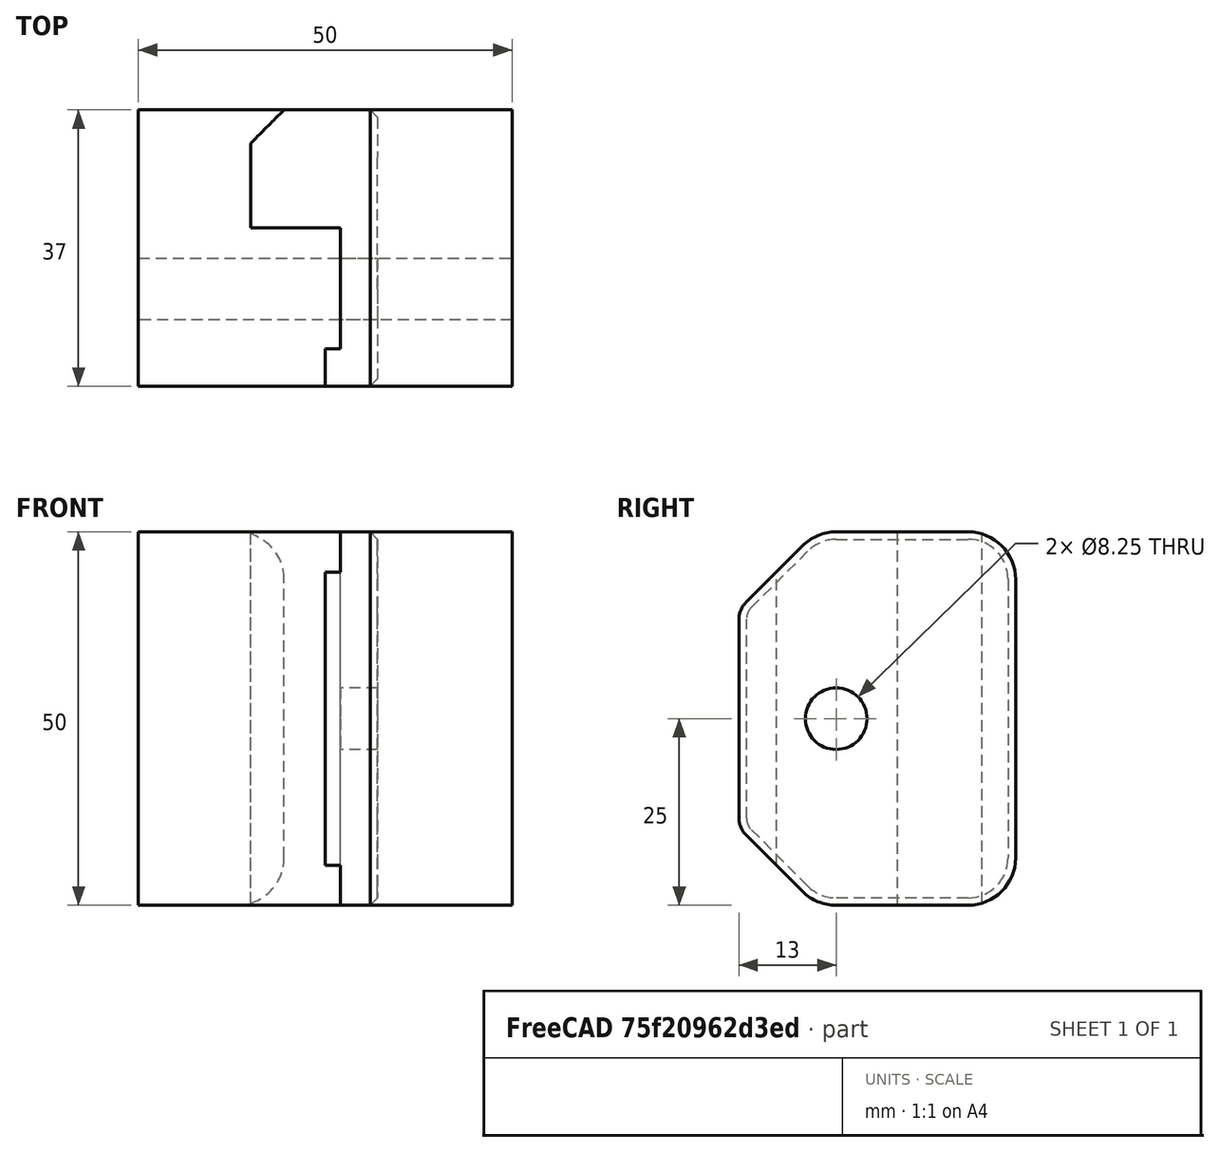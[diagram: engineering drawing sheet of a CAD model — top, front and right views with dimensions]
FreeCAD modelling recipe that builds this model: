
FCSTD DOCUMENT  (FreeCAD 0.19R23578 (Git))
Label: z_rail_clamp
License: All rights reserved
LicenseURL: http://en.wikipedia.org/wiki/All_rights_reserved
objects: TechDraw::DrawViewDimension×14, TechDraw::DrawProjGroupItem×3, Sketcher::SketchObject×2, PartDesign::Pad×2, PartDesign::Body×2, PartDesign::Boolean×1, PartDesign::Chamfer×1, App::Part×1, TechDraw::DrawSVGTemplate×1, TechDraw::DrawViewPart×1, TechDraw::DrawProjGroup×1, TechDraw::DrawPage×1
note: 11 computed .brp shape members not serialized (recipe doc carries the construction recipe); baked Part::Feature solids carry a one-line shape summary decoded from their .brp

FEATURE [Sketcher::SketchObject] Sketch073
  MapMode = 5
  Support = -> [XY_Plane086]
  sketch-geometry (14):
    g0: LineSegment StartX=0 StartY=0 StartZ=0 EndX=0 EndY=-9.5892e-11 EndZ=0
    g1: LineSegment StartX=0 StartY=0 StartZ=0 EndX=-18 EndY=0 EndZ=0
    g2: LineSegment StartX=-18 StartY=0 StartZ=0 EndX=-18 EndY=20 EndZ=0
    g3: LineSegment StartX=-18 StartY=20 StartZ=0 EndX=0 EndY=20 EndZ=0
    g4: Circle CenterX=-12 CenterY=14 CenterZ=0 NormalX=0 NormalY=0 NormalZ=1 AngleXU=0 Radius=6
    g5: LineSegment StartX=7 StartY=12 StartZ=0 EndX=-5.51472 EndY=12 EndZ=0
    g6: LineSegment StartX=-5.51472 StartY=12 StartZ=0 EndX=-10 EndY=7.51472 EndZ=0
    g7: LineSegment StartX=-10 StartY=7.51472 StartZ=0 EndX=-10 EndY=-3.8 EndZ=0
    g8: LineSegment StartX=-10 StartY=-3.8 StartZ=0 EndX=2 EndY=-3.8 EndZ=0
    g9: LineSegment StartX=2 StartY=-3.8 StartZ=0 EndX=2 EndY=-20 EndZ=0
    g10: LineSegment StartX=2 StartY=-20 StartZ=0 EndX=0 EndY=-20 EndZ=0
    g11: LineSegment StartX=0 StartY=-20 StartZ=0 EndX=0 EndY=-40 EndZ=0
    g12: LineSegment StartX=0 StartY=-40 StartZ=0 EndX=7 EndY=-40 EndZ=0
    g13: LineSegment StartX=7 StartY=-40 StartZ=0 EndX=7 EndY=12 EndZ=0
  constraints (41):
    c: Coincident(g0,g-1)
    c: Coincident(g1,g-1)
    c: PointOnObject(g1,g-1)
    c: Coincident(g2,g1)
    c: Vertical(g2)
    c: Coincident(g3,g2)
    c: PointOnObject(g3,g-2)
    c: Horizontal(g3)
    c: Tangent(g4,g3)
    c: Tangent(g4,g2)
    c: Diameter(g4) = 12
    c: DistanceX(g3,g3) = 18
    c: DistanceY(g2,g2) = 20
    c: Horizontal(g5)
    c: Coincident(g5,g6)
    c: Tangent(g6,g4)
    c: Coincident(g6,g7)
    c: Vertical(g7)
    c: Coincident(g7,g8)
    c: Horizontal(g8)
    c: Coincident(g8,g9)
    c: Vertical(g9)
    c: Coincident(g9,g10)
    c: Horizontal(g10)
    c: Coincident(g10,g11)
    c: Coincident(g11,g12)
    c: Horizontal(g12)
    c: Coincident(g12,g13)
    c: Coincident(g13,g5)
    c: Vertical(g13)
    c: Angle(g8,g6) = 0.785398
    c: DistanceY(g-1,g5) = 12
    c: DistanceX(g10,g10) = 2
    c: DistanceX(g12,g12) = 7
    c: DistanceY(g9,g9) = 16.2
    c: DistanceY(g11,g11) = 20
    c: Coincident(g0,g-1)
    c: Vertical(g11)
    c: PointOnObject(g10,g-2)
    c: DistanceX(g7,g-1) = 10
    c: DistanceY(g7,g2) = 23.8
FEATURE [PartDesign::Pad] Pad027  label="Pad028"
  Direction = (1,1,1)
  Length = 100
  Length2 = 100
  Midplane = true
  Profile = -> Sketch073
  Type = 0
FEATURE [Sketcher::SketchObject] Sketch074
  MapMode = 5
  Placement = pos=(0,0,0) rot=(0.57735,0.57735,0.57735;2.0944rad)
  Support = -> [YZ_Plane085]
  sketch-geometry (13):
    g0: LineSegment StartX=12 StartY=18.65 StartZ=0 EndX=12 EndY=-18.65 EndZ=0
    g1: LineSegment StartX=5.65 StartY=-25 StartZ=0 EndX=-12 EndY=-25 EndZ=0
    g2: LineSegment StartX=-16.4901 StartY=-23.1401 StartZ=0 EndX=-24.092 EndY=-15.5382 EndZ=0
    g3: LineSegment StartX=-24.092 StartY=15.5382 StartZ=0 EndX=-16.4901 EndY=23.1401 EndZ=0
    g4: LineSegment StartX=-12 StartY=25 StartZ=0 EndX=5.65 EndY=25 EndZ=0
    g5: ArcOfCircle CenterX=5.65 CenterY=18.65 CenterZ=0 NormalX=0 NormalY=0 NormalZ=1 AngleXU=0 Radius=6.35 StartAngle=0 EndAngle=1.5708
    g6: ArcOfCircle CenterX=-12 CenterY=18.65 CenterZ=0 NormalX=0 NormalY=0 NormalZ=1 AngleXU=0 Radius=6.35 StartAngle=1.5708 EndAngle=2.35619
    g7: ArcOfCircle CenterX=-12 CenterY=-18.65 CenterZ=0 NormalX=0 NormalY=0 NormalZ=1 AngleXU=0 Radius=6.35 StartAngle=3.92699 EndAngle=4.71239
    g8: ArcOfCircle CenterX=5.65 CenterY=-18.65 CenterZ=0 NormalX=0 NormalY=0 NormalZ=1 AngleXU=0 Radius=6.35 StartAngle=4.71239 EndAngle=6.28319
    g9: Circle CenterX=-12 CenterY=0 CenterZ=0 NormalX=0 NormalY=0 NormalZ=1 AngleXU=0 Radius=4.125
    g10: LineSegment StartX=-25 StartY=13.3462 StartZ=0 EndX=-25 EndY=-13.3462 EndZ=0
    g11: ArcOfCircle CenterX=-21.9 CenterY=13.3462 CenterZ=0 NormalX=0 NormalY=0 NormalZ=1 AngleXU=0 Radius=3.1 StartAngle=2.35619 EndAngle=3.14159
    g12: ArcOfCircle CenterX=-21.9 CenterY=-13.3462 CenterZ=0 NormalX=0 NormalY=0 NormalZ=1 AngleXU=0 Radius=3.1 StartAngle=3.14159 EndAngle=3.92699
  constraints (30):
    c: Vertical(g0)
    c: Horizontal(g1)
    c: Tangent(g4,g5) = 1.5708
    c: Tangent(g0,g5) = 1.5708
    c: Tangent(g4,g6) = 1.5708
    c: Tangent(g3,g6) = 1.5708
    c: Tangent(g2,g7) = 1.5708
    c: Tangent(g1,g7) = 1.5708
    c: Tangent(g0,g8) = 1.5708
    c: Tangent(g1,g8) = 1.5708
    c: Horizontal(g4)
    c: Equal(g7,g8)
    c: Symmetric(g4,g1,g-1)
    c: Symmetric(g6,g7,g-1)
    c: PointOnObject(g9,g-1)
    c: DistanceY(g1,g4) = 50
    c: Radius(g5) = 6.35
    c: Diameter(g9) = 8.25
    c: DistanceX(g-1,g0) = 12
    c: Angle(g2,g3) = 1.5708
    c: Vertical(g10)
    c: Tangent(g3,g11) = 1.5708
    c: Tangent(g10,g11) = -1.5708
    c: Tangent(g10,g12) = -1.5708
    c: Tangent(g2,g12) = 1.5708
    c: Radius(g11) = 3.1
    c: Symmetric(g11,g12,g-1)
    c: DistanceX(g10,g-1) = 25
    c: Vertical(g7,g9)
    c: DistanceX(g9,g-1) = 12
FEATURE [PartDesign::Pad] Pad028  label="Pad029"
  Direction = (1,1,1)
  Length = 50
  Length2 = 100
  Midplane = true
  Placement = pos=(0,0,0) rot=(0.57735,0.57735,0.57735;2.0944rad)
  Profile = -> Sketch074
  Type = 0
FEATURE [PartDesign::Body] Body028
  Group = -> [Sketch074,Pad028]
  Origin = -> Origin085
  Tip = -> Pad028
FEATURE [PartDesign::Boolean] Boolean002
  BaseFeature = -> Pad027
  Group = -> [Body028]
  Type = 2
FEATURE [PartDesign::Chamfer] Chamfer002
  Angle = 45
  Base = -> Boolean002 [Edge14]
  BaseFeature = -> Boolean002
  ChamferType = 0
  FlipDirection = false
  Size = 1
  Size2 = 1
  SupportTransform = true
FEATURE [PartDesign::Body] Body029  label="Body"
  Group = -> [Sketch073,Pad027,Boolean002,Chamfer002]
  Origin = -> Origin086
  Tip = -> Chamfer002
FEATURE [App::Part] Part044  label="z_rail_clamp"
  Group = -> [Body029]
  Origin = -> Origin082
FEATURE [TechDraw::DrawSVGTemplate] Template003
  EditableTexts = Author=Alex Neufeld; DWG_num=2020-102; Date=15/05/2020; Revision=2; Scale=NTS; Subtitle=4 Req.; Title=12mm Shaft Clamp
  Height = 215.9
  Orientation = 1
  Width = 279.4
FEATURE [TechDraw::DrawViewPart] View003
  CoarseView = false
  Direction = (0.577,-0.577,0.577)
  Focus = 100
  HardHidden = false
  IsoCount = 0
  IsoHidden = false
  IsoVisible = false
  LockPosition = false
  Perspective = false
  Rotation = 0
  Scale = 0.5
  ScaleType = 0
  SeamHidden = false
  SeamVisible = true
  SmoothHidden = false
  SmoothVisible = true
  Source = -> [Body029]
  X = 33.5005
  XDirection = (0.707,0.707,0)
  Y = 183.223
FEATURE [TechDraw::DrawProjGroupItem] ProjItem014  label="Front003"
  CoarseView = false
  Direction = (1,0,0)
  Focus = 100
  HardHidden = false
  IsoCount = 0
  IsoHidden = false
  IsoVisible = false
  LockPosition = true
  Perspective = false
  Rotation = 0
  RotationVector = (0,1,0)
  ScaleType = 2
  SeamHidden = false
  SeamVisible = true
  SmoothHidden = false
  SmoothVisible = true
  Source = -> [Body029]
  Type = 0
  X = 0
  XDirection = (0,1,0)
  Y = 0
FEATURE [TechDraw::DrawProjGroupItem] ProjItem015  label="Bottom003"
  CoarseView = false
  Direction = (0,0,-1)
  Focus = 100
  HardHidden = false
  IsoCount = 0
  IsoHidden = false
  IsoVisible = false
  LockPosition = false
  Perspective = false
  Rotation = 0
  RotationVector = (1,0,0)
  ScaleType = 2
  SeamHidden = false
  SeamVisible = true
  SmoothHidden = false
  SmoothVisible = true
  Source = -> [Body029]
  Type = 5
  X = 0
  XDirection = (0,1,0)
  Y = 48.5
FEATURE [TechDraw::DrawProjGroupItem] ProjItem016  label="Left002"
  CoarseView = false
  Direction = (1e-16,-1,0)
  Focus = 100
  HardHidden = false
  IsoCount = 0
  IsoHidden = false
  IsoVisible = false
  LockPosition = false
  Perspective = false
  Rotation = 0
  RotationVector = (1,0,0)
  ScaleType = 2
  SeamHidden = false
  SeamVisible = true
  SmoothHidden = false
  SmoothVisible = true
  Source = -> [Body029]
  Type = 1
  X = 42
  XDirection = (1,1e-16,0)
  Y = 0
FEATURE [TechDraw::DrawProjGroup] ProjGroup003
  Anchor = -> ProjItem014
  AutoDistribute = true
  LockPosition = false
  ProjectionType = 0
  Rotation = 0
  ScaleType = 0
  Source = -> [Body029]
  Views = -> [ProjItem014,ProjItem015,ProjItem016]
  X = 116.598
  Y = 88.1517
  spacingX = 15
  spacingY = 15
FEATURE [TechDraw::DrawViewDimension] Dimension065
  Arbitrary = false
  ArbitraryTolerances = false
  FormatSpec = %.2f
  FormatSpecOverTolerance = %+.2f
  FormatSpecUnderTolerance = %+.2f
  Inverted = false
  LockPosition = false
  MeasureType = 1
  OverTolerance = 0
  References2D = -> [ProjItem014]
  Rotation = 0
  ScaleType = 0
  TheoreticalExact = false
  Type = 2
  UnderTolerance = 0
  X = -37.8717
  Y = 1.13496
FEATURE [TechDraw::DrawViewDimension] Dimension066
  Arbitrary = false
  ArbitraryTolerances = false
  FormatSpec = %.2f
  FormatSpecOverTolerance = %+.2f
  FormatSpecUnderTolerance = %+.2f
  Inverted = false
  LockPosition = false
  MeasureType = 1
  OverTolerance = 0
  References2D = -> [ProjItem014]
  Rotation = 0
  ScaleType = 0
  TheoreticalExact = false
  Type = 1
  UnderTolerance = 0
  X = 0.243131
  Y = 37.6367
FEATURE [TechDraw::DrawViewDimension] Dimension067
  Arbitrary = false
  ArbitraryTolerances = false
  FormatSpec = %.2f
  FormatSpecOverTolerance = %+.2f
  FormatSpecUnderTolerance = %+.2f
  Inverted = false
  LockPosition = false
  MeasureType = 1
  OverTolerance = 0
  References2D = -> [ProjItem016]
  Rotation = 0
  ScaleType = 0
  TheoreticalExact = false
  Type = 1
  UnderTolerance = 0
  X = 0
  Y = 39.0878
FEATURE [TechDraw::DrawViewDimension] Dimension071
  Arbitrary = false
  ArbitraryTolerances = false
  FormatSpec = R%.2f
  FormatSpecOverTolerance = %+.2f
  FormatSpecUnderTolerance = %+.2f
  Inverted = false
  LockPosition = false
  MeasureType = 1
  OverTolerance = 0
  References2D = -> [ProjItem014]
  Rotation = 0
  ScaleType = 0
  TheoreticalExact = false
  Type = 4
  UnderTolerance = 0
  X = 26.3188
  Y = -26.8506
FEATURE [TechDraw::DrawViewDimension] Dimension072
  Arbitrary = false
  ArbitraryTolerances = false
  FormatSpec = %.2f
  FormatSpecOverTolerance = %+.2f
  FormatSpecUnderTolerance = %+.2f
  Inverted = false
  LockPosition = false
  MeasureType = 1
  OverTolerance = 0
  References2D = -> [ProjItem014]
  Rotation = 0
  ScaleType = 0
  TheoreticalExact = false
  Type = 2
  UnderTolerance = 0
  X = -29.7505
  Y = 14.0649
FEATURE [TechDraw::DrawViewDimension] Dimension073
  Arbitrary = false
  ArbitraryTolerances = false
  FormatSpec = %.2f
  FormatSpecOverTolerance = %+.2f
  FormatSpecUnderTolerance = %+.2f
  Inverted = false
  LockPosition = false
  MeasureType = 1
  OverTolerance = 0
  References2D = -> [ProjItem014]
  Rotation = 0
  ScaleType = 0
  TheoreticalExact = false
  Type = 1
  UnderTolerance = 0
  X = 6.85175
  Y = 30.4524
FEATURE [TechDraw::DrawViewDimension] Dimension074
  Arbitrary = false
  ArbitraryTolerances = false
  FormatSpec = %.2f
  FormatSpecOverTolerance = %+.2f
  FormatSpecUnderTolerance = %+.2f
  Inverted = false
  LockPosition = false
  MeasureType = 1
  OverTolerance = 0
  References2D = -> [ProjItem015]
  Rotation = 0
  ScaleType = 0
  TheoreticalExact = false
  Type = 2
  UnderTolerance = 0
  X = 30.2019
  Y = 19.9033
FEATURE [TechDraw::DrawViewDimension] Dimension075
  Arbitrary = false
  ArbitraryTolerances = false
  FormatSpec = %.2f
  FormatSpecOverTolerance = %+.2f
  FormatSpecUnderTolerance = %+.2f
  Inverted = false
  LockPosition = false
  MeasureType = 1
  OverTolerance = 0
  References2D = -> [ProjItem016]
  Rotation = 0
  ScaleType = 0
  TheoreticalExact = false
  Type = 1
  UnderTolerance = 0
  X = 21.6334
  Y = -26.5519
FEATURE [TechDraw::DrawViewDimension] Dimension076
  Arbitrary = false
  ArbitraryTolerances = false
  FormatSpec = %.2f
  FormatSpecOverTolerance = %+.2f
  FormatSpecUnderTolerance = %+.2f
  Inverted = false
  LockPosition = false
  MeasureType = 1
  OverTolerance = 0
  References2D = -> [ProjItem016]
  Rotation = 0
  ScaleType = 0
  TheoreticalExact = false
  Type = 1
  UnderTolerance = 0
  X = 21.8059
  Y = -36.276
FEATURE [TechDraw::DrawViewDimension] Dimension077
  Arbitrary = false
  ArbitraryTolerances = false
  FormatSpec = %.2f
  FormatSpecOverTolerance = %+.2f
  FormatSpecUnderTolerance = %+.2f
  Inverted = false
  LockPosition = false
  MeasureType = 1
  OverTolerance = 0
  References2D = -> [ProjItem015]
  Rotation = 0
  ScaleType = 0
  TheoreticalExact = false
  Type = 1
  UnderTolerance = 0
  X = -3.60183
  Y = 32.5074
FEATURE [TechDraw::DrawViewDimension] Dimension078
  Arbitrary = false
  ArbitraryTolerances = false
  FormatSpec = %.2f
  FormatSpecOverTolerance = %+.2f
  FormatSpecUnderTolerance = %+.2f
  Inverted = false
  LockPosition = false
  MeasureType = 1
  OverTolerance = 0
  References2D = -> [ProjItem015]
  Rotation = 0
  ScaleType = 0
  TheoreticalExact = false
  Type = 1
  UnderTolerance = 0
  X = -2.87816
  Y = 24.8554
FEATURE [TechDraw::DrawViewDimension] Dimension079
  Arbitrary = false
  ArbitraryTolerances = false
  FormatSpec = %.2f
  FormatSpecOverTolerance = %+.2f
  FormatSpecUnderTolerance = %+.2f
  Inverted = false
  LockPosition = false
  MeasureType = 1
  OverTolerance = 0
  References2D = -> [ProjItem015]
  Rotation = 0
  ScaleType = 0
  TheoreticalExact = false
  Type = 1
  UnderTolerance = 0
  X = -2.68862
  Y = 15.912
FEATURE [TechDraw::DrawViewDimension] Dimension080
  Arbitrary = false
  ArbitraryTolerances = false
  FormatSpec = ⌀%.2f
  FormatSpecOverTolerance = %+.2f
  FormatSpecUnderTolerance = %+.2f
  Inverted = false
  LockPosition = false
  MeasureType = 1
  OverTolerance = 0
  References2D = -> [ProjItem014]
  Rotation = 0
  ScaleType = 0
  TheoreticalExact = false
  Type = 5
  UnderTolerance = 0
  X = 1.86435
  Y = 11.9851
FEATURE [TechDraw::DrawViewDimension] Dimension081
  Arbitrary = false
  ArbitraryTolerances = false
  FormatSpec = %.2f
  FormatSpecOverTolerance = %+.2f
  FormatSpecUnderTolerance = %+.2f
  Inverted = false
  LockPosition = false
  MeasureType = 1
  OverTolerance = 0
  References2D = -> [ProjItem016]
  Rotation = 0
  ScaleType = 0
  TheoreticalExact = false
  Type = 1
  UnderTolerance = 0
  X = 22.9956
  Y = 31.5567
FEATURE [TechDraw::DrawPage] Page003  label="shaft_clamp_dwg"
  KeepUpdated = false
  NextBalloonIndex = 1
  ProjectionType = 0
  Template = -> Template003
  Views = -> [View003,ProjGroup003,Dimension065,Dimension066,Dimension067,Dimension071,Dimension072,Dimension073,Dimension074,Dimension075,Dimension076,Dimension077,Dimension078,Dimension079,Dimension080,Dimension081]
